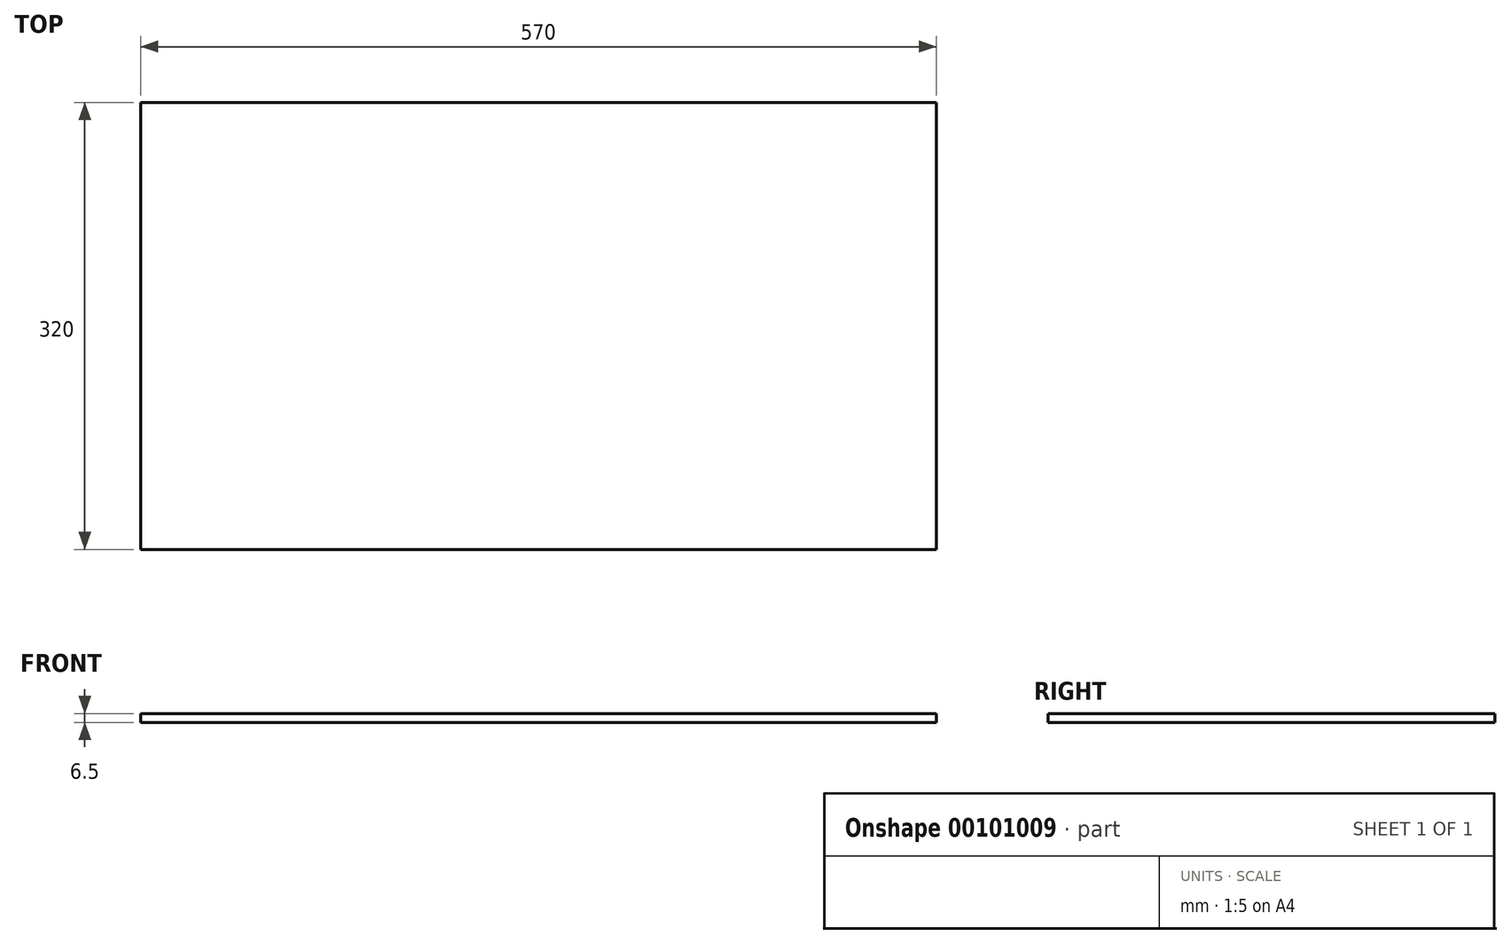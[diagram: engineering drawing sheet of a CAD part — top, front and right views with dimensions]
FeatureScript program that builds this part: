
annotation { "Feature Type Name" : "Feature", "Feature Type Description" : "" }
export const myFeature = defineFeature(function(context is Context, id is Id, definition is map)
    precondition{}
    {
        {
            var Q0;
            Q0=qCreatedBy(makeId("Top.planeOp"),FACE);
            var sketch = newSketch(context, id + "F0", { "sketchPlane" : qUnion([Q0])});
            skLineSegment(sketch, "E0.bottom", {"start": v(0, 0) * mm, "end": v(570, 0) * mm});
            skLineSegment(sketch, "E0.top", {"start": v(0, 320) * mm, "end": v(570, 320) * mm});
            skLineSegment(sketch, "E0.left", {"start": v(0, 0) * mm, "end": v(0, 320) * mm});
            skLineSegment(sketch, "E0.right", {"start": v(570, 0) * mm, "end": v(570, 320) * mm});
            skSolve(sketch);
        }
        {
            var Q0;
            Q0 = qSketchRegion(id + "F0", true);
            extrude(context, id + "F1", {"entities" : qUnion([Q0]), "depth" : 6.5 * mm});
        }
    });
